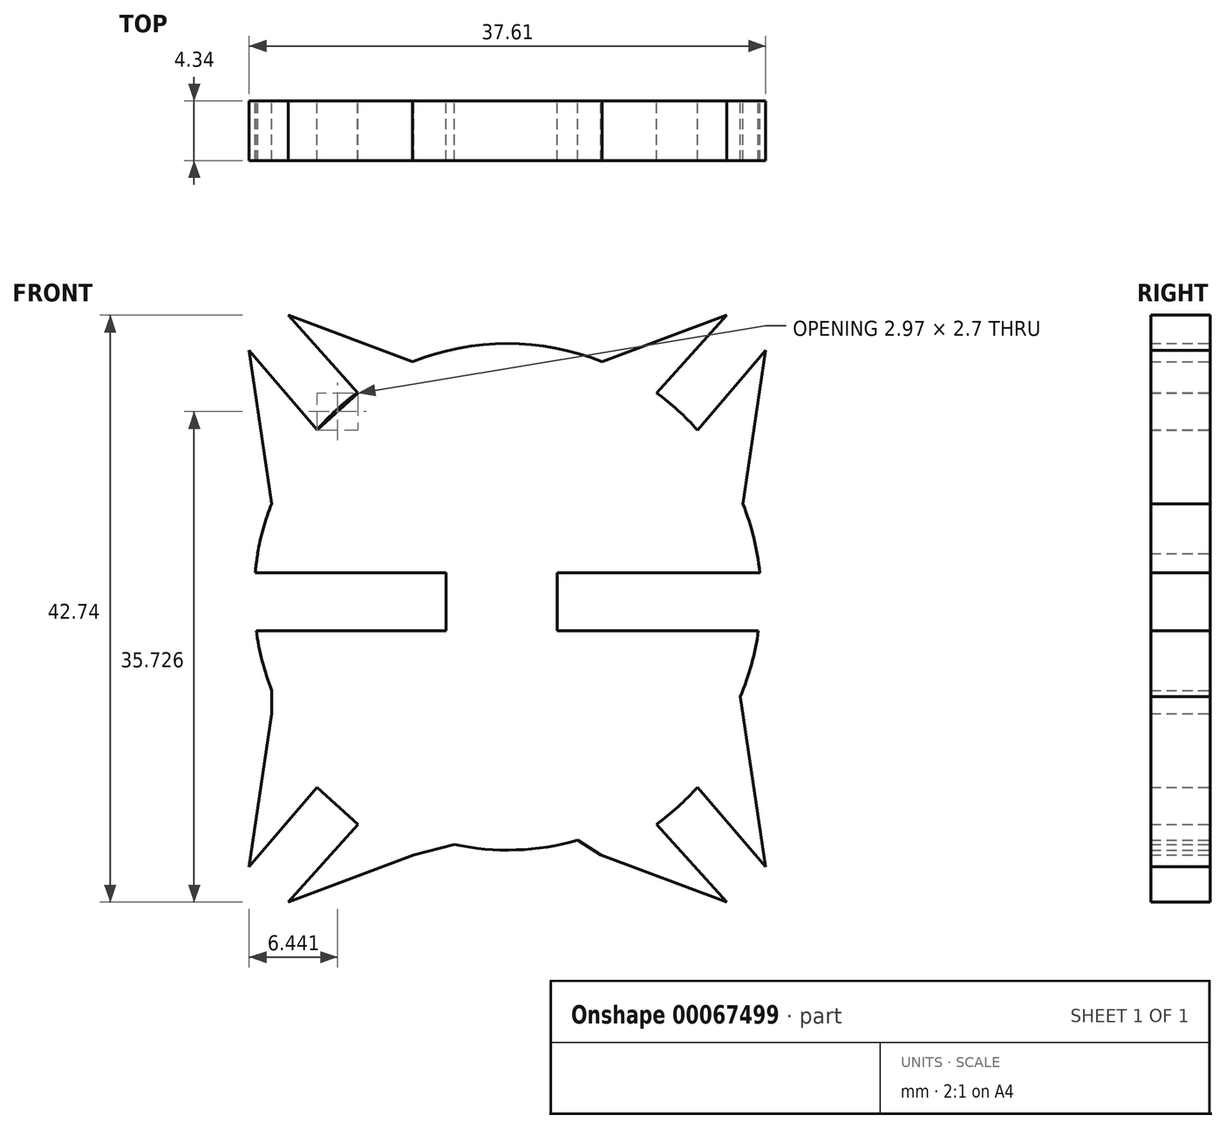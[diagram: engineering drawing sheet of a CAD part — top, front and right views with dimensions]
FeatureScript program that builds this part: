
annotation { "Feature Type Name" : "Feature", "Feature Type Description" : "" }
export const myFeature = defineFeature(function(context is Context, id is Id, definition is map)
    precondition{}
    {
        {
            var Q0;
            Q0=qCreatedBy(makeId("Front.planeOp"),FACE);
            var sketch = newSketch(context, id + "F0", { "sketchPlane" : qUnion([Q0])});
            skArc(sketch, "E0.trimOffspring", {"start": v(-5.85, -11.1) * mm, "mid": v(-5.82, -11.11) * mm, "end": v(-5.8, -11.13) * mm});
            skPoint(sketch, "E1.startSnap0", {"position": v(-12.7, -0.16) * mm});
            skLineSegment(sketch, "E2.MirrorCS", {"start": v(-7.88, -9.91) * mm, "end": v(-8.3, -9.47) * mm});
            skPoint(sketch, "E1.start.orphan", {"position": v(-12.7, 0) * mm});
            skLineSegment(sketch, "E3.MirrorCS", {"start": v(7.88, -9.91) * mm, "end": v(8.3, -9.47) * mm});
            skPoint(sketch, "E4.orphan", {"position": v(-15.1, 11.34) * mm});
            skPoint(sketch, "E5.MirrorCS.end.orphan", {"position": v(9.38, 12.1) * mm});
            skPoint(sketch, "E5.MirrorCS.start.orphan", {"position": v(14.33, 10.09) * mm});
            skPoint(sketch, "E6.orphan", {"position": v(15.1, 11.34) * mm});
            skPoint(sketch, "E7.MirrorCS.end.orphan", {"position": v(11.58, -13.2) * mm});
            skPoint(sketch, "E7.MirrorCS.start.orphan", {"position": v(11.94, -12.83) * mm});
            skPoint(sketch, "E8.orphan", {"position": v(12.02, -13.36) * mm});
            skPoint(sketch, "E9.MirrorCS.end.orphan", {"position": v(-11.58, -13.2) * mm});
            skPoint(sketch, "E9.MirrorCS.start.orphan", {"position": v(-11.94, -12.83) * mm});
            skPoint(sketch, "E10.orphan", {"position": v(-12.02, -13.36) * mm});
            skPoint(sketch, "E11.orphan", {"position": v(-5.8, -11.13) * mm});
            skPoint(sketch, "E12.orphan", {"position": v(5.93, -11.27) * mm});
            skPoint(sketch, "E13.orphan", {"position": v(10.99, -6.37) * mm});
            skPoint(sketch, "E14.start.orphan", {"position": v(-6.32, 1.27) * mm});
            skLineSegment(sketch, "E15", {"start": v(4.14, -0.78) * mm, "end": v(4.14, 1.27) * mm});
            skPoint(sketch, "E16.orphan", {"position": v(0, -1.27) * mm});
            skPoint(sketch, "E17.orphan", {"position": v(0, 1.27) * mm});
            skPoint(sketch, "E18.MirrorCS.end.orphan", {"position": v(-9.38, 12.1) * mm});
            skPoint(sketch, "E19.MirrorCS.end.orphan", {"position": v(7.13, 9.87) * mm});
            skPoint(sketch, "E20.MirrorCS.start.orphan", {"position": v(10.14, 6.74) * mm});
            skPoint(sketch, "E21.MirrorCS.end.orphan", {"position": v(-11.14, -6.09) * mm});
            skPoint(sketch, "E22.MirrorCS.start.orphan", {"position": v(-8.3, -9.47) * mm});
            skPoint(sketch, "E23.MirrorCS.end.orphan", {"position": v(-7.88, -9.91) * mm});
            skPoint(sketch, "E24.MirrorCS.end.orphan", {"position": v(7.88, -9.91) * mm});
            skPoint(sketch, "E25.MirrorCS.start.orphan", {"position": v(8.3, -9.47) * mm});
            skArc(sketch, "E26.trimOffspring", {"start": v(-11.14, -6.09) * mm, "mid": v(-11.07, -6.23) * mm, "end": v(-10.99, -6.37) * mm});
            skPoint(sketch, "E27.orphan", {"position": v(11.14, -6.09) * mm});
            skPoint(sketch, "E28.end.orphan", {"position": v(4.14, 0) * mm});
            skPoint(sketch, "E29.orphan", {"position": v(0, 12.7) * mm});
            skPoint(sketch, "E30.start.orphan", {"position": v(34.11, -14.77) * mm});
            skLineSegment(sketch, "E31", {"start": v(15.72, -31.4) * mm, "end": v(29.64, -31.4) * mm});
            skLineSegment(sketch, "E32", {"start": v(15.83, -35.62) * mm, "end": v(29.64, -35.62) * mm});
            skPoint(sketch, "E33.start.orphan", {"position": v(17.48, -25.23) * mm});
            skLineSegment(sketch, "E34", {"start": v(34.11, -33.27) * mm, "end": v(34.11, -33.52) * mm});
            skPoint(sketch, "E35", {"position": v(34.11, -33.52) * mm});
            skArc(sketch, "E36.trimOffspring", {"start": v(52.5, -31.4) * mm, "mid": v(52.06, -28.85) * mm, "end": v(51.27, -26.39) * mm});
            skLineSegment(sketch, "E37", {"start": v(29.64, -31.4) * mm, "end": v(29.64, -35.62) * mm});
            skLineSegment(sketch, "E38", {"start": v(37.74, -31.4) * mm, "end": v(37.74, -35.62) * mm});
            skPoint(sketch, "E39.orphan", {"position": v(34.11, -31.4) * mm});
            skPoint(sketch, "E40.orphan", {"position": v(34.11, -35.62) * mm});
            skLineSegment(sketch, "E41", {"start": v(37.74, -33.52) * mm, "end": v(38.02, -33.52) * mm});
            skPoint(sketch, "E42.orphan", {"position": v(29.64, -33.52) * mm});
            skLineSegment(sketch, "E43.trimOffspring", {"start": v(37.74, -35.62) * mm, "end": v(52.4, -35.62) * mm});
            skLineSegment(sketch, "E44.trimOffspring", {"start": v(37.74, -31.4) * mm, "end": v(52.5, -31.4) * mm});
            skPoint(sketch, "E45.start.orphan", {"position": v(-8.63, 8.3) * mm});
            skLineSegment(sketch, "E46", {"start": v(16.96, -26.39) * mm, "end": v(15.3, -15.24) * mm});
            skLineSegment(sketch, "E47", {"start": v(15.3, -15.24) * mm, "end": v(20.27, -21.02) * mm});
            skLineSegment(sketch, "E48", {"start": v(23.24, -18.32) * mm, "end": v(18.14, -12.66) * mm});
            skLineSegment(sketch, "E49", {"start": v(18.14, -12.66) * mm, "end": v(27.3, -16.09) * mm});
            skArc(sketch, "E50.trimOffspring", {"start": v(16.96, -26.39) * mm, "mid": v(16.34, -28.18) * mm, "end": v(15.92, -30.02) * mm});
            skArc(sketch, "E51.trimOffspring", {"start": v(23.24, -18.32) * mm, "mid": v(21.68, -19.6) * mm, "end": v(20.27, -21.02) * mm});
            skLineSegment(sketch, "E52", {"start": v(34.11, -14.77) * mm, "end": v(34.11, -51.66) * mm, "construction": true});
            skLineSegment(sketch, "E53.MirrorCS", {"start": v(44.99, -18.32) * mm, "end": v(50.08, -12.66) * mm});
            skLineSegment(sketch, "E54.MirrorCS", {"start": v(50.08, -12.66) * mm, "end": v(40.93, -16.09) * mm});
            skLineSegment(sketch, "E55.MirrorCS", {"start": v(51.27, -26.39) * mm, "end": v(52.92, -15.24) * mm});
            skLineSegment(sketch, "E56.MirrorCS", {"start": v(52.92, -15.24) * mm, "end": v(47.96, -21.02) * mm});
            skPoint(sketch, "E57.MirrorCS.end.orphan", {"position": v(47.96, -21.02) * mm});
            skPoint(sketch, "E57.MirrorCS.start.orphan", {"position": v(44.99, -18.32) * mm});
            skArc(sketch, "E58.trimOffspring", {"start": v(5.93, -11.27) * mm, "mid": v(5.96, -11.25) * mm, "end": v(5.98, -11.24) * mm});
            skPoint(sketch, "E59.end.orphan", {"position": v(-156.17, -33.52) * mm});
            skPoint(sketch, "E60.orphan", {"position": v(-10.14, 6.74) * mm});
            skPoint(sketch, "E61.start.orphan", {"position": v(-7.13, 9.87) * mm});
            skLineSegment(sketch, "E62", {"start": v(20.27, -21.02) * mm, "end": v(23.24, -18.32) * mm});
            skPoint(sketch, "E63.end.orphan", {"position": v(20.75, -15.55) * mm});
            skPoint(sketch, "E63.start.orphan", {"position": v(17.79, -18.13) * mm});
            skPoint(sketch, "E64.MirrorCS.end.orphan", {"position": v(47.48, -15.55) * mm});
            skPoint(sketch, "E64.MirrorCS.start.orphan", {"position": v(50.44, -18.13) * mm});
            skPoint(sketch, "E65.MirrorCS.end.orphan", {"position": v(47.45, -51.02) * mm});
            skPoint(sketch, "E65.MirrorCS.start.orphan", {"position": v(50.46, -48.31) * mm});
            skPoint(sketch, "E66.MirrorCS.end.orphan", {"position": v(20.83, -51.02) * mm});
            skPoint(sketch, "E66.MirrorCS.start.orphan", {"position": v(17.81, -48.31) * mm});
            skPoint(sketch, "E67.trimOffspring.end.orphan", {"position": v(52.5, -42.06) * mm});
            skArc(sketch, "E68.trimOffspring", {"start": v(40.93, -16.09) * mm, "mid": v(34.11, -14.78) * mm, "end": v(27.3, -16.09) * mm});
            skArc(sketch, "E69.trimOffspring", {"start": v(47.96, -21.02) * mm, "mid": v(46.55, -19.6) * mm, "end": v(44.99, -18.32) * mm});
            skPoint(sketch, "E70.MirrorCS.end.orphan", {"position": v(40.93, -50.44) * mm});
            skLineSegment(sketch, "E71", {"start": v(40.93, -50.35) * mm, "end": v(40.95, -50.34) * mm});
            skPoint(sketch, "E72.orphan", {"position": v(25, -49.24) * mm});
            skPoint(sketch, "E73.center.orphan", {"position": v(34.11, -25.23) * mm});
            skArc(sketch, "E74.MirrorCS", {"start": v(20.25, -21) * mm, "mid": v(21.66, -19.57) * mm, "end": v(23.2, -18.3) * mm});
            skLineSegment(sketch, "E75.MirrorCS", {"start": v(15.92, -30.02) * mm, "end": v(15.94, -30.02) * mm});
            skLineSegment(sketch, "E76.MirrorCS", {"start": v(15.94, -30.02) * mm, "end": v(15.94, -30.08) * mm});
            skArc(sketch, "E77.MirrorCS", {"start": v(15.75, -31.4) * mm, "mid": v(15.83, -30.71) * mm, "end": v(15.94, -30.02) * mm});
            skArc(sketch, "E78.MirrorCS", {"start": v(34.11, -51.67) * mm, "mid": v(31.67, -51.5) * mm, "end": v(29.27, -51.02) * mm});
            skPoint(sketch, "E79.orphan", {"position": v(21.21, -19.99) * mm});
            skPoint(sketch, "E80.MirrorCS.start.orphan", {"position": v(28.02, -58.53) * mm});
            skPoint(sketch, "E81.MirrorCS.start.orphan", {"position": v(29.27, -51.02) * mm});
            skPoint(sketch, "E82.MirrorCS.start.orphan", {"position": v(33.23, -51.65) * mm});
            skPoint(sketch, "E83.MirrorCS.start.orphan", {"position": v(31.81, -59.14) * mm});
            skPoint(sketch, "E84.MirrorCS.start.orphan", {"position": v(39.49, -50.88) * mm});
            skArc(sketch, "E85.MirrorCS", {"start": v(52.4, -35.62) * mm, "mid": v(51.9, -38.08) * mm, "end": v(51.08, -40.44) * mm});
            skArc(sketch, "E86.MirrorCS", {"start": v(33.23, -51.65) * mm, "mid": v(31.24, -51.44) * mm, "end": v(29.27, -51.02) * mm});
            skArc(sketch, "E87.MirrorCS", {"start": v(16.96, -39.98) * mm, "mid": v(16.7, -39.3) * mm, "end": v(16.47, -38.6) * mm});
            skPoint(sketch, "E88.orphan", {"position": v(18.06, -24.09) * mm});
            skPoint(sketch, "E89.MirrorCS.end.orphan", {"position": v(8.33, -29.76) * mm});
            skPoint(sketch, "E90.orphan", {"position": v(18.06, -24.1) * mm});
            skPoint(sketch, "E91.MirrorCS.end.orphan", {"position": v(8.08, -33.59) * mm});
            skPoint(sketch, "E91.MirrorCS.start.orphan", {"position": v(15.69, -34.03) * mm});
            skPoint(sketch, "E92.MirrorCS.end.orphan", {"position": v(16.47, -38.6) * mm});
            skArc(sketch, "E93.trimOffspring", {"start": v(52.4, -35.62) * mm, "mid": v(51.9, -38.06) * mm, "end": v(51.08, -40.41) * mm});
            skArc(sketch, "E94.trimOffspring", {"start": v(15.76, -31.4) * mm, "mid": v(16.53, -27.63) * mm, "end": v(18.06, -24.1) * mm});
            skArc(sketch, "E95.trimOffspring", {"start": v(20.25, -21) * mm, "mid": v(20.72, -20.49) * mm, "end": v(21.21, -19.99) * mm});
            skArc(sketch, "E96.trimOffspring", {"start": v(27.22, -16.06) * mm, "mid": v(34.12, -14.72) * mm, "end": v(41.01, -16.06) * mm});
            skLineSegment(sketch, "E97", {"start": v(15.69, -34.03) * mm, "end": v(52.83, -34.03) * mm});
            skLineSegment(sketch, "E98.MirrorCS", {"start": v(16.96, -41.67) * mm, "end": v(15.3, -52.81) * mm});
            skLineSegment(sketch, "E99.MirrorCS", {"start": v(15.3, -52.81) * mm, "end": v(20.27, -47.03) * mm});
            skLineSegment(sketch, "E100.MirrorCS", {"start": v(20.27, -47.03) * mm, "end": v(23.24, -49.73) * mm});
            skPoint(sketch, "E101.MirrorP", {"position": v(20.75, -52.5) * mm});
            skLineSegment(sketch, "E102.MirrorCS", {"start": v(23.24, -49.73) * mm, "end": v(18.14, -55.4) * mm});
            skLineSegment(sketch, "E103.MirrorCS", {"start": v(18.14, -55.4) * mm, "end": v(27.3, -51.96) * mm});
            skLineSegment(sketch, "E104.MirrorCS", {"start": v(50.08, -55.4) * mm, "end": v(40.93, -51.96) * mm});
            skLineSegment(sketch, "E105.MirrorCS", {"start": v(44.99, -49.73) * mm, "end": v(50.08, -55.4) * mm});
            skArc(sketch, "E106.MirrorCS", {"start": v(47.96, -47.03) * mm, "mid": v(46.55, -48.46) * mm, "end": v(44.99, -49.73) * mm});
            skLineSegment(sketch, "E107.MirrorCS", {"start": v(52.92, -52.81) * mm, "end": v(47.96, -47.03) * mm});
            skLineSegment(sketch, "E108.MirrorCS", {"start": v(51.27, -41.67) * mm, "end": v(52.92, -52.81) * mm});
            skLineSegment(sketch, "E109", {"start": v(16.96, -41.67) * mm, "end": v(16.96, -39.98) * mm});
            skLineSegment(sketch, "E110", {"start": v(27.3, -51.96) * mm, "end": v(30.24, -51.2) * mm});
            skArc(sketch, "E111.trimOffspring", {"start": v(16.96, -39.98) * mm, "mid": v(16.26, -37.84) * mm, "end": v(15.83, -35.62) * mm});
            skLineSegment(sketch, "E112", {"start": v(40.93, -51.96) * mm, "end": v(39.23, -50.88) * mm});
            skLineSegment(sketch, "E113", {"start": v(51.27, -41.67) * mm, "end": v(51.08, -40.41) * mm});
            skArc(sketch, "E114.trimOffspring", {"start": v(39.23, -50.88) * mm, "mid": v(34.75, -51.6) * mm, "end": v(30.24, -51.2) * mm});
            skSolve(sketch);
        }
        {
            var Q0;
            Q0 = qSketchRegion(id + "F0", true);
            extrude(context, id + "F1", {"entities" : qUnion([Q0]), "depth" : 4.34 * mm});
        }
    });
